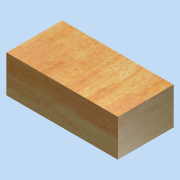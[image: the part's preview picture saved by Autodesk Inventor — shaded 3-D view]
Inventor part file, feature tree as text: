
AUTODESK INVENTOR PART (.ipt)
format: ipt  version: 2014 (Build 180170000, 170)  size: 111,616 bytes
history: native  units: in
note: dims shown in document units (in); Inventor stores cm internally (conversion verified against a paired STEP export)
features: extrude x1, sketch x1
ambient origin geometry x8: Origin, YZ Plane, XZ Plane, XY Plane, X Axis, Y Axis, Z Axis, Center Point
bodies: Solid1 (feature_tree)
feature tree (2):
  extrude  "Extrusion1"  Depth=0.5in
  sketch  "Sketch1"  dims[d0=1.5in d1=0.5in d2=0.75in d3=0.0in]
